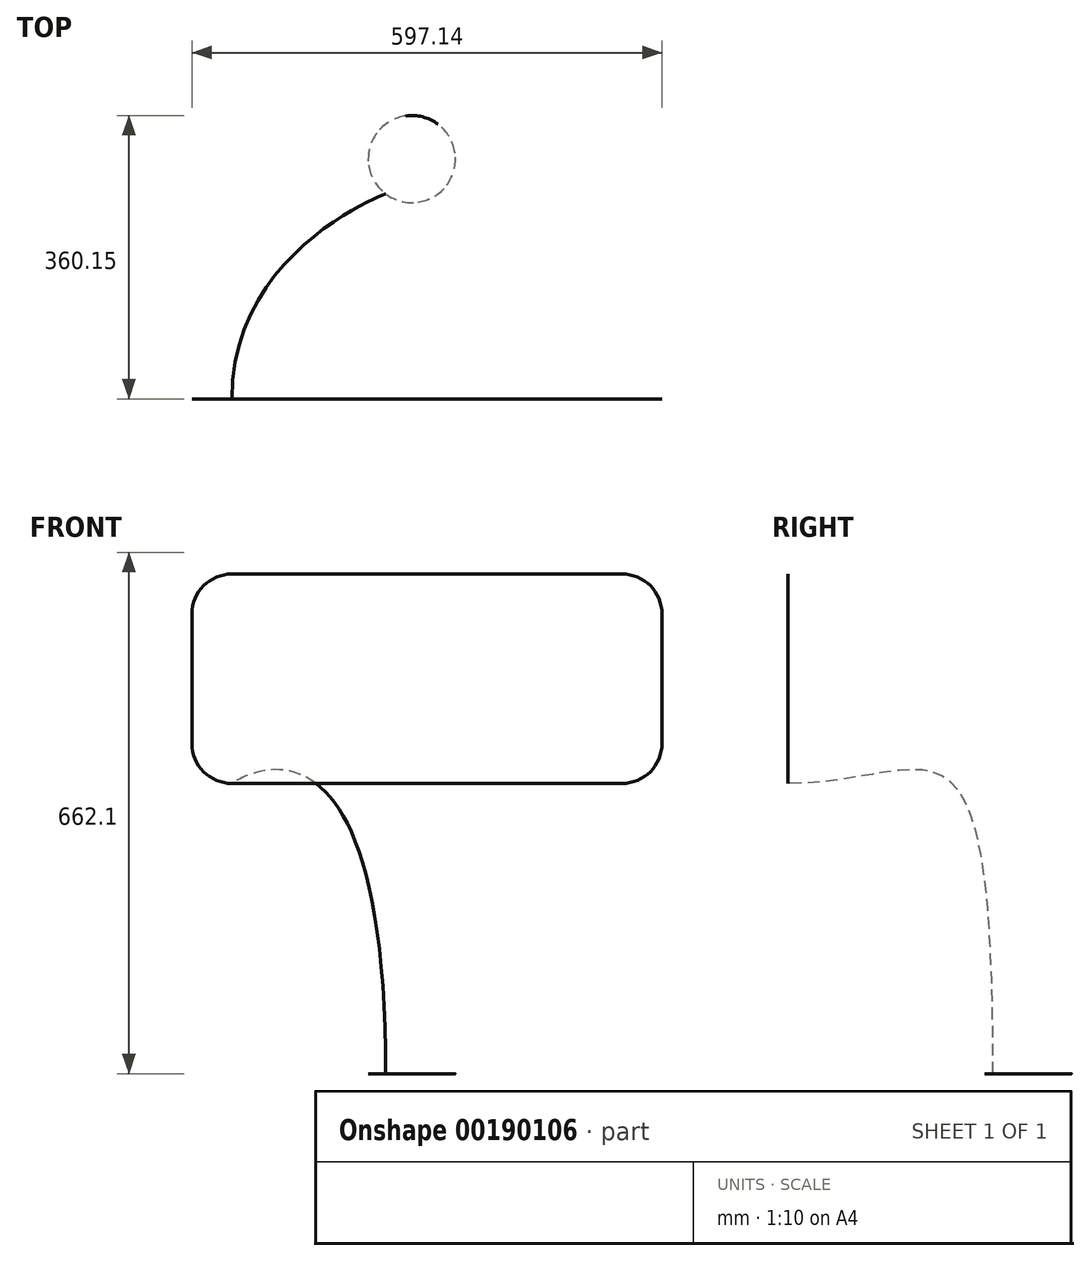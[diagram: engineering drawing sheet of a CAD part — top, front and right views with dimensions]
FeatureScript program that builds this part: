
annotation { "Feature Type Name" : "Feature", "Feature Type Description" : "" }
export const myFeature = defineFeature(function(context is Context, id is Id, definition is map)
    precondition{}
    {
        {
            var Q0;
            Q0=qCreatedBy(makeId("Top.planeOp"),FACE);
            var sketch = newSketch(context, id + "F0", { "sketchPlane" : qUnion([Q0])});
            skCircle(sketch, "E0", {"center": v(0, 0) * mm, "radius": 55.35 * mm});
            skPoint(sketch, "E1", {"position": v(55.35, 0) * mm});
            skPoint(sketch, "E2", {"position": v(0, -55.35) * mm});
            skPoint(sketch, "E3", {"position": v(-55.35, 0) * mm});
            skPoint(sketch, "E4", {"position": v(0, 55.35) * mm});
            skSolve(sketch);
        }
        {
            var Q0;
            Q0=qCreatedBy(makeId("Front.planeOp"),FACE);
            cPlane(context, id + "F1", {"entities" : qUnion([Q0]), "cplaneType" : CPlaneType.OFFSET, "offset" : 304.8 * mm, "width" : 152.4 * mm, "height" : 152.4 * mm});
        }
        {
            var Q0;
            Q0=qCreatedBy(id+"F1.planeOp",FACE);
            var sketch = newSketch(context, id + "F2", { "sketchPlane" : qUnion([Q0])});
            skLineSegment(sketch, "E5.bottom", {"start": v(-228.53, 634.7) * mm, "end": v(267, 634.7) * mm});
            skLineSegment(sketch, "E5.top", {"start": v(-228.53, 368.7) * mm, "end": v(267, 368.7) * mm});
            skLineSegment(sketch, "E5.left", {"start": v(-279.33, 583.9) * mm, "end": v(-279.33, 419.5) * mm});
            skLineSegment(sketch, "E5.right", {"start": v(317.8, 583.9) * mm, "end": v(317.8, 419.5) * mm});
            skPoint(sketch, "E6.visualSharp", {"position": v(-279.33, 634.7) * mm});
            skArc(sketch, "E6.filletArc", {"start": v(-228.53, 634.7) * mm, "mid": v(-264.45, 619.83) * mm, "end": v(-279.33, 583.9) * mm});
            skPoint(sketch, "E7.visualSharp", {"position": v(317.8, 634.7) * mm});
            skArc(sketch, "E7.filletArc", {"start": v(317.8, 583.9) * mm, "mid": v(302.93, 619.83) * mm, "end": v(267, 634.7) * mm});
            skPoint(sketch, "E8.visualSharp", {"position": v(317.8, 368.7) * mm});
            skArc(sketch, "E8.filletArc", {"start": v(267, 368.7) * mm, "mid": v(302.93, 383.58) * mm, "end": v(317.8, 419.5) * mm});
            skPoint(sketch, "E9.visualSharp", {"position": v(-279.33, 368.7) * mm});
            skArc(sketch, "E9.filletArc", {"start": v(-279.33, 419.5) * mm, "mid": v(-264.45, 383.58) * mm, "end": v(-228.53, 368.7) * mm});
            skPoint(sketch, "E10", {"position": v(0, 368.7) * mm});
            skPoint(sketch, "E11", {"position": v(0, 634.7) * mm});
            skPoint(sketch, "E12", {"position": v(317.8, 501.7) * mm});
            skPoint(sketch, "E13", {"position": v(-279.33, 501.7) * mm});
            skSolve(sketch);
        }
        {
            var Q0;
            Q0=makeQuery(id+"F0.imprint","IMPRINT",FACE,{"disambiguationData":[TD([[makeQuery(id+"F0.imprint","IMPRINT",EDGE,{"derivedFrom":sQuery(id+"F0.wireOp",EDGE,"E0")}),1.0]])]});
            var Q1;
            Q1=makeQuery(id+"F2.imprint","IMPRINT",FACE,{"disambiguationData":[TD([[makeQuery(id+"F2.imprint","IMPRINT",EDGE,{"derivedFrom":sQuery(id+"F2.wireOp",EDGE,"E5.bottom")}),-1.0]])]});
            loft(context, id + "F3", {"startCondition" : LoftEndDerivativeType.NORMAL_TO_PROFILE, "startMagnitude" : 4, "endCondition" : LoftEndDerivativeType.NORMAL_TO_PROFILE, "endMagnitude" : 2, "sheetProfilesArray" : [{ "sheetProfileEntities" : qUnion([Q0]) }, { "sheetProfileEntities" : qUnion([Q1]) }]});
        }
    });
